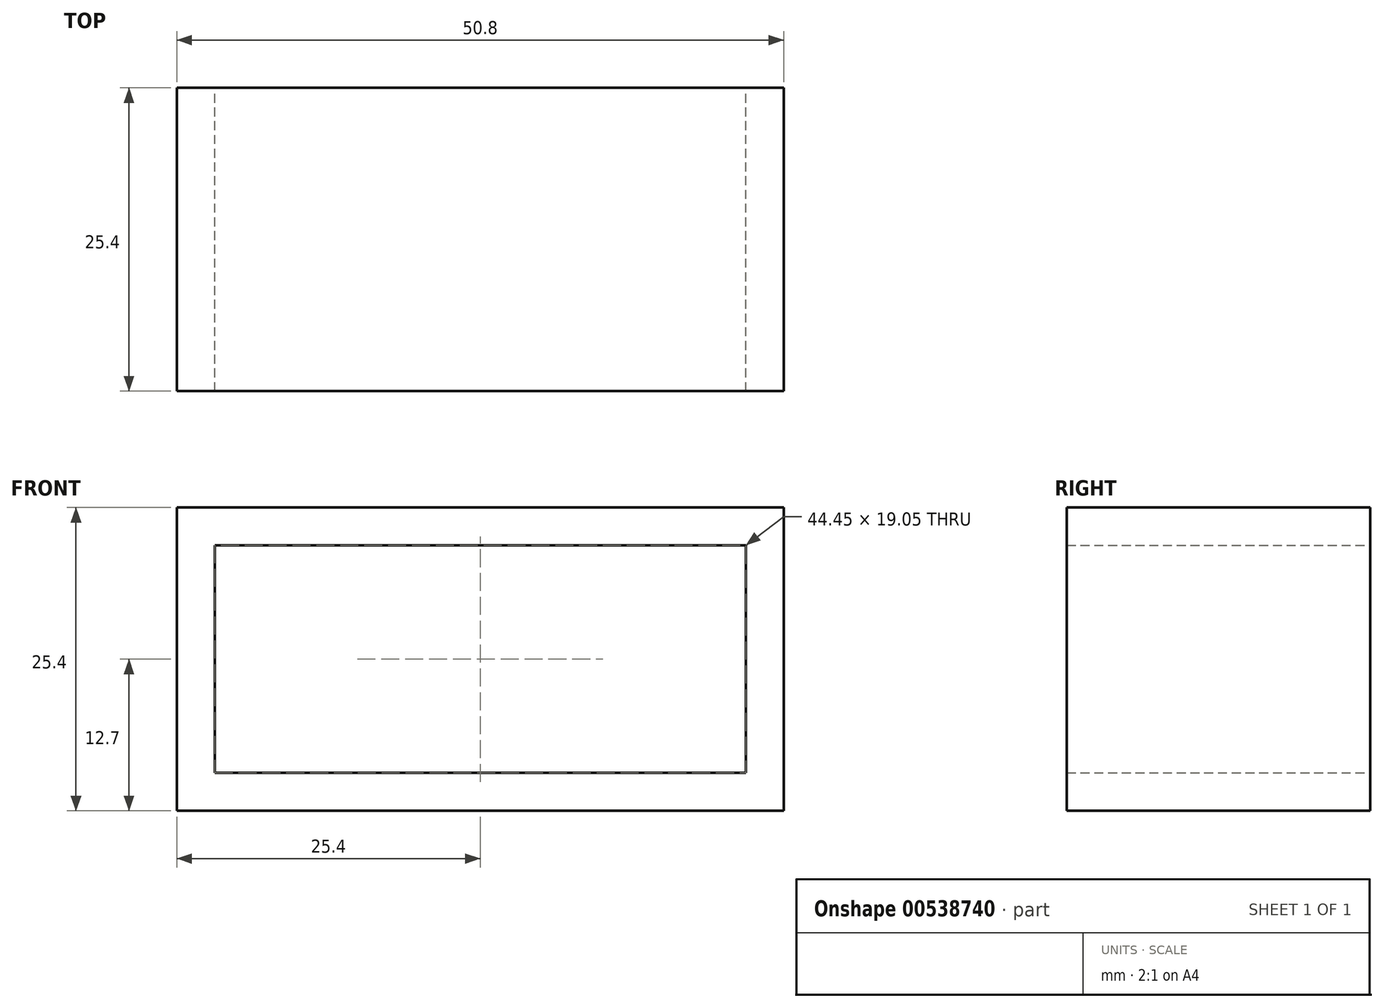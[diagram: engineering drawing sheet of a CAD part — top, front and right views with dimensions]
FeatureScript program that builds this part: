
annotation { "Feature Type Name" : "Feature", "Feature Type Description" : "" }
export const myFeature = defineFeature(function(context is Context, id is Id, definition is map)
    precondition{}
    {
        {
            var Q0;
            Q0=qCreatedBy(makeId("Front.planeOp"),FACE);
            var sketch = newSketch(context, id + "F0", { "sketchPlane" : qUnion([Q0])});
            skLineSegment(sketch, "E0.bottom", {"start": v(0, 0) * mm, "end": v(50.8, 0) * mm});
            skLineSegment(sketch, "E0.top", {"start": v(0, -25.4) * mm, "end": v(50.8, -25.4) * mm});
            skLineSegment(sketch, "E0.left", {"start": v(0, 0) * mm, "end": v(0, -25.4) * mm});
            skLineSegment(sketch, "E0.right", {"start": v(50.8, 0) * mm, "end": v(50.8, -25.4) * mm});
            skLineSegment(sketch, "E1.bottom", {"start": v(3.18, -3.18) * mm, "end": v(47.63, -3.18) * mm});
            skLineSegment(sketch, "E1.top", {"start": v(3.18, -22.23) * mm, "end": v(47.63, -22.23) * mm});
            skLineSegment(sketch, "E1.left", {"start": v(3.18, -3.18) * mm, "end": v(3.18, -22.23) * mm});
            skLineSegment(sketch, "E1.right", {"start": v(47.63, -3.18) * mm, "end": v(47.63, -22.23) * mm});
            skSolve(sketch);
        }
        {
            var Q0;
            Q0=makeQuery(id+"F0.imprint","IMPRINT",FACE,{"disambiguationData":[TD([[makeQuery(id+"F0.imprint","IMPRINT",EDGE,{"derivedFrom":sQuery(id+"F0.wireOp",EDGE,"E0.bottom")}),-1.0]])]});
            extrude(context, id + "F1", {"entities" : qUnion([Q0]), "depth" : 25.4 * mm, "offsetDistance" : 25.4 * mm});
        }
    });
